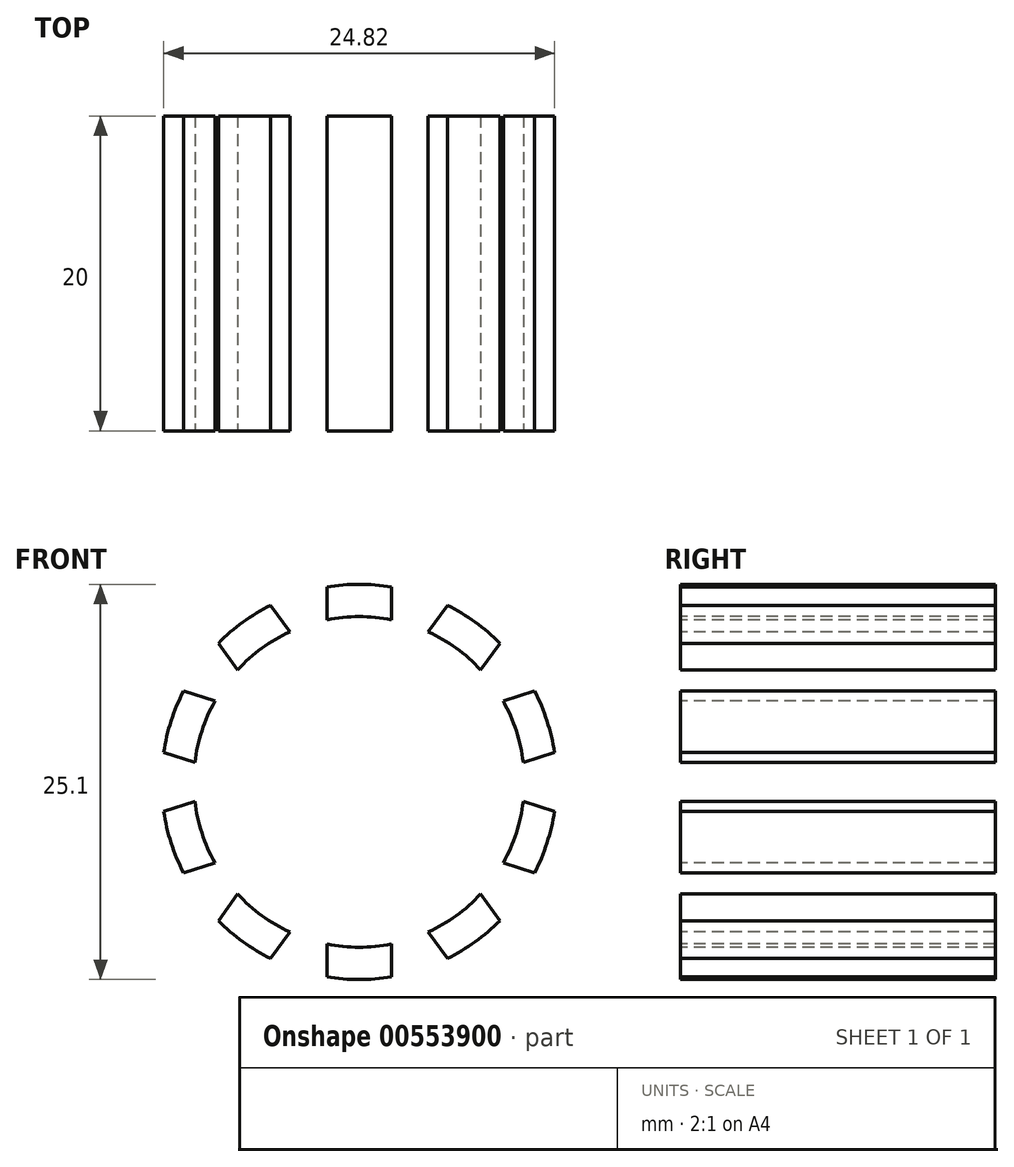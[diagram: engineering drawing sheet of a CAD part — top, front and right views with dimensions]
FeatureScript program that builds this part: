
annotation { "Feature Type Name" : "Feature", "Feature Type Description" : "" }
export const myFeature = defineFeature(function(context is Context, id is Id, definition is map)
    precondition{}
    {
        {
            var Q0;
            Q0=qCreatedBy(makeId("Front.planeOp"),FACE);
            var sketch = newSketch(context, id + "F0", { "sketchPlane" : qUnion([Q0])});
            skCircle(sketch, "E0", {"center": v(0, 0) * mm, "radius": 50 * mm});
            skLineSegment(sketch, "E1", {"start": v(0, 46.5) * mm, "end": v(83.9, 46.5) * mm, "construction": true});
            skLineSegment(sketch, "E2", {"start": v(0, 50) * mm, "end": v(23.37, 50) * mm, "construction": true});
            skArc(sketch, "E3.trimOffspring", {"start": v(-5.04, 60.29) * mm, "mid": v(-5.7, 54.98) * mm, "end": v(-6.05, 49.63) * mm});
            skLineSegment(sketch, "E4", {"start": v(0, 50) * mm, "end": v(0, 60.5) * mm});
            skArc(sketch, "E5.trimOffspring", {"start": v(0, 60.5) * mm, "mid": v(-2.52, 60.45) * mm, "end": v(-5.04, 60.29) * mm});
            skArc(sketch, "E6.MirrorCS", {"start": v(0, 60.5) * mm, "mid": v(2.52, 60.45) * mm, "end": v(5.04, 60.29) * mm});
            skArc(sketch, "E7.MirrorCS", {"start": v(5.04, 60.29) * mm, "mid": v(5.7, 54.98) * mm, "end": v(6.05, 49.63) * mm});
            skArc(sketch, "E8.1.0", {"start": v(-29.12, 53.03) * mm, "mid": v(-27.57, 47.9) * mm, "end": v(-25.71, 42.88) * mm});
            skArc(sketch, "E8.1.1", {"start": v(-24.6, 55.27) * mm, "mid": v(-26.89, 54.2) * mm, "end": v(-29.12, 53.03) * mm});
            skArc(sketch, "E8.1.2", {"start": v(-24.6, 55.27) * mm, "mid": v(-22.28, 56.25) * mm, "end": v(-19.92, 57.13) * mm});
            skArc(sketch, "E8.1.3", {"start": v(-19.92, 57.13) * mm, "mid": v(-17.15, 52.54) * mm, "end": v(-14.66, 47.8) * mm});
            skArc(sketch, "E9.3.2.0", {"start": v(-48.17, 36.6) * mm, "mid": v(-44.67, 32.55) * mm, "end": v(-40.93, 28.72) * mm});
            skArc(sketch, "E9.4.2.0", {"start": v(-44.96, 40.48) * mm, "mid": v(-46.6, 38.57) * mm, "end": v(-48.17, 36.6) * mm});
            skArc(sketch, "E9.8.2.0", {"start": v(-44.96, 40.48) * mm, "mid": v(-43.23, 42.32) * mm, "end": v(-41.43, 44.09) * mm});
            skArc(sketch, "E9.12.2.0", {"start": v(-41.43, 44.09) * mm, "mid": v(-37.04, 41.02) * mm, "end": v(-32.84, 37.7) * mm});
            skArc(sketch, "E9.3.3.0", {"start": v(-58.9, 13.84) * mm, "mid": v(-54.05, 11.57) * mm, "end": v(-49.07, 9.59) * mm});
            skArc(sketch, "E9.4.3.0", {"start": v(-57.54, 18.7) * mm, "mid": v(-58.27, 16.28) * mm, "end": v(-58.9, 13.84) * mm});
            skArc(sketch, "E9.8.3.0", {"start": v(-57.54, 18.7) * mm, "mid": v(-56.7, 21.08) * mm, "end": v(-55.78, 23.42) * mm});
            skArc(sketch, "E9.12.3.0", {"start": v(-55.78, 23.42) * mm, "mid": v(-50.52, 22.4) * mm, "end": v(-45.34, 21.09) * mm});
            skArc(sketch, "E9.3.4.0", {"start": v(-59.43, -11.31) * mm, "mid": v(-54.08, -11.42) * mm, "end": v(-48.73, -11.2) * mm});
            skArc(sketch, "E9.4.4.0", {"start": v(-60.17, -6.32) * mm, "mid": v(-59.85, -8.83) * mm, "end": v(-59.43, -11.31) * mm});
            skArc(sketch, "E9.8.4.0", {"start": v(-60.17, -6.32) * mm, "mid": v(-60.38, -3.81) * mm, "end": v(-60.49, -1.3) * mm});
            skArc(sketch, "E9.12.4.0", {"start": v(-60.49, -1.3) * mm, "mid": v(-55.27, -0.08) * mm, "end": v(-50, 0.82) * mm});
            skArc(sketch, "E9.3.5.0", {"start": v(-49.7, -34.5) * mm, "mid": v(-44.76, -32.42) * mm, "end": v(-39.96, -30.05) * mm});
            skArc(sketch, "E9.4.5.0", {"start": v(-52.4, -30.25) * mm, "mid": v(-51.09, -32.4) * mm, "end": v(-49.7, -34.5) * mm});
            skArc(sketch, "E9.8.5.0", {"start": v(-52.4, -30.25) * mm, "mid": v(-53.6, -28.04) * mm, "end": v(-54.73, -25.78) * mm});
            skArc(sketch, "E9.12.5.0", {"start": v(-54.73, -25.78) * mm, "mid": v(-50.46, -22.55) * mm, "end": v(-46, -19.58) * mm});
            skArc(sketch, "E9.3.6.0", {"start": v(-31.36, -51.74) * mm, "mid": v(-27.7, -47.83) * mm, "end": v(-24.28, -43.7) * mm});
            skArc(sketch, "E9.4.6.0", {"start": v(-35.56, -48.95) * mm, "mid": v(-33.5, -50.38) * mm, "end": v(-31.36, -51.74) * mm});
            skArc(sketch, "E9.8.6.0", {"start": v(-35.56, -48.95) * mm, "mid": v(-37.57, -47.42) * mm, "end": v(-39.51, -45.81) * mm});
            skArc(sketch, "E9.12.6.0", {"start": v(-39.51, -45.81) * mm, "mid": v(-36.93, -41.13) * mm, "end": v(-34.06, -36.6) * mm});
            skArc(sketch, "E9.3.7.0", {"start": v(-7.6, -60.02) * mm, "mid": v(-5.85, -54.96) * mm, "end": v(-4.4, -49.8) * mm});
            skArc(sketch, "E9.4.7.0", {"start": v(-12.58, -59.18) * mm, "mid": v(-10.1, -59.65) * mm, "end": v(-7.6, -60.02) * mm});
            skArc(sketch, "E9.8.7.0", {"start": v(-12.58, -59.18) * mm, "mid": v(-15.03, -58.6) * mm, "end": v(-17.46, -57.93) * mm});
            skArc(sketch, "E9.12.7.0", {"start": v(-17.46, -57.93) * mm, "mid": v(-17, -52.6) * mm, "end": v(-16.23, -47.3) * mm});
            skArc(sketch, "E9.3.8.0", {"start": v(17.46, -57.93) * mm, "mid": v(17, -52.6) * mm, "end": v(16.23, -47.3) * mm});
            skArc(sketch, "E9.4.8.0", {"start": v(12.58, -59.18) * mm, "mid": v(15.03, -58.6) * mm, "end": v(17.46, -57.93) * mm});
            skArc(sketch, "E9.8.8.0", {"start": v(12.58, -59.18) * mm, "mid": v(10.1, -59.65) * mm, "end": v(7.6, -60.02) * mm});
            skArc(sketch, "E9.12.8.0", {"start": v(7.6, -60.02) * mm, "mid": v(5.85, -54.96) * mm, "end": v(4.4, -49.8) * mm});
            skArc(sketch, "E9.3.9.0", {"start": v(39.51, -45.81) * mm, "mid": v(36.93, -41.13) * mm, "end": v(34.06, -36.6) * mm});
            skArc(sketch, "E9.4.9.0", {"start": v(35.56, -48.95) * mm, "mid": v(37.57, -47.42) * mm, "end": v(39.51, -45.81) * mm});
            skArc(sketch, "E9.8.9.0", {"start": v(35.56, -48.95) * mm, "mid": v(33.5, -50.38) * mm, "end": v(31.36, -51.74) * mm});
            skArc(sketch, "E9.12.9.0", {"start": v(31.36, -51.74) * mm, "mid": v(27.7, -47.83) * mm, "end": v(24.28, -43.7) * mm});
            skArc(sketch, "E9.3.10.0", {"start": v(54.73, -25.78) * mm, "mid": v(50.46, -22.55) * mm, "end": v(46, -19.58) * mm});
            skArc(sketch, "E9.4.10.0", {"start": v(52.4, -30.25) * mm, "mid": v(53.6, -28.04) * mm, "end": v(54.73, -25.78) * mm});
            skArc(sketch, "E9.8.10.0", {"start": v(52.4, -30.25) * mm, "mid": v(51.09, -32.4) * mm, "end": v(49.7, -34.5) * mm});
            skArc(sketch, "E9.12.10.0", {"start": v(49.7, -34.5) * mm, "mid": v(44.76, -32.42) * mm, "end": v(39.96, -30.05) * mm});
            skArc(sketch, "E9.3.11.0", {"start": v(60.49, -1.3) * mm, "mid": v(55.27, -0.08) * mm, "end": v(50, 0.82) * mm});
            skArc(sketch, "E9.4.11.0", {"start": v(60.17, -6.32) * mm, "mid": v(60.38, -3.81) * mm, "end": v(60.49, -1.3) * mm});
            skArc(sketch, "E9.8.11.0", {"start": v(60.17, -6.32) * mm, "mid": v(59.85, -8.83) * mm, "end": v(59.43, -11.31) * mm});
            skArc(sketch, "E9.12.11.0", {"start": v(59.43, -11.31) * mm, "mid": v(54.08, -11.42) * mm, "end": v(48.73, -11.2) * mm});
            skArc(sketch, "E9.3.12.0", {"start": v(55.78, 23.42) * mm, "mid": v(50.52, 22.4) * mm, "end": v(45.34, 21.09) * mm});
            skArc(sketch, "E9.4.12.0", {"start": v(57.54, 18.7) * mm, "mid": v(56.7, 21.08) * mm, "end": v(55.78, 23.42) * mm});
            skArc(sketch, "E9.8.12.0", {"start": v(57.54, 18.7) * mm, "mid": v(58.27, 16.28) * mm, "end": v(58.9, 13.84) * mm});
            skArc(sketch, "E9.12.12.0", {"start": v(58.9, 13.84) * mm, "mid": v(54.05, 11.57) * mm, "end": v(49.07, 9.59) * mm});
            skArc(sketch, "E9.3.13.0", {"start": v(41.43, 44.09) * mm, "mid": v(37.04, 41.02) * mm, "end": v(32.84, 37.7) * mm});
            skArc(sketch, "E9.4.13.0", {"start": v(44.96, 40.48) * mm, "mid": v(43.23, 42.32) * mm, "end": v(41.43, 44.09) * mm});
            skArc(sketch, "E9.8.13.0", {"start": v(44.96, 40.48) * mm, "mid": v(46.6, 38.57) * mm, "end": v(48.17, 36.6) * mm});
            skArc(sketch, "E9.12.13.0", {"start": v(48.17, 36.6) * mm, "mid": v(44.67, 32.55) * mm, "end": v(40.93, 28.72) * mm});
            skArc(sketch, "E9.3.14.0", {"start": v(19.92, 57.13) * mm, "mid": v(17.15, 52.54) * mm, "end": v(14.66, 47.8) * mm});
            skArc(sketch, "E9.4.14.0", {"start": v(24.6, 55.27) * mm, "mid": v(22.28, 56.25) * mm, "end": v(19.92, 57.13) * mm});
            skArc(sketch, "E9.8.14.0", {"start": v(24.6, 55.27) * mm, "mid": v(26.89, 54.2) * mm, "end": v(29.12, 53.03) * mm});
            skArc(sketch, "E9.12.14.0", {"start": v(29.12, 53.03) * mm, "mid": v(27.57, 47.9) * mm, "end": v(25.71, 42.88) * mm});
            skSolve(sketch);
        }
        {
            var Q0;
            Q0 = qSketchRegion(id + "F0", true);
            extrude(context, id + "F1", {"entities" : qUnion([Q0]), "depth" : 20 * mm, "offsetDistance" : 25 * mm});
        }
        {
            var Q0;
            Q0=makeQuery(id+"F1.opExtrude","CAP_FACE",FACE,{"disambiguationData":[OSD([sQuery(id+"F0.wireOp",EDGE,"E0"),sQuery(id+"F0.wireOp",EDGE,"E3.trimOffspring"),sQuery(id+"F0.wireOp",EDGE,"E5.trimOffspring"),sQuery(id+"F0.wireOp",EDGE,"E6.MirrorCS"),sQuery(id+"F0.wireOp",EDGE,"E7.MirrorCS"),sQuery(id+"F0.wireOp",EDGE,"E8.1.0"),sQuery(id+"F0.wireOp",EDGE,"E8.1.1"),sQuery(id+"F0.wireOp",EDGE,"E8.1.2"),sQuery(id+"F0.wireOp",EDGE,"E8.1.3"),sQuery(id+"F0.wireOp",EDGE,"E9.3.2.0"),sQuery(id+"F0.wireOp",EDGE,"E9.4.2.0"),sQuery(id+"F0.wireOp",EDGE,"E9.8.2.0"),sQuery(id+"F0.wireOp",EDGE,"E9.12.2.0"),sQuery(id+"F0.wireOp",EDGE,"E9.3.3.0"),sQuery(id+"F0.wireOp",EDGE,"E9.4.3.0"),sQuery(id+"F0.wireOp",EDGE,"E9.8.3.0"),sQuery(id+"F0.wireOp",EDGE,"E9.12.3.0"),sQuery(id+"F0.wireOp",EDGE,"E9.3.4.0"),sQuery(id+"F0.wireOp",EDGE,"E9.4.4.0"),sQuery(id+"F0.wireOp",EDGE,"E9.8.4.0"),sQuery(id+"F0.wireOp",EDGE,"E9.12.4.0"),sQuery(id+"F0.wireOp",EDGE,"E9.3.5.0"),sQuery(id+"F0.wireOp",EDGE,"E9.4.5.0"),sQuery(id+"F0.wireOp",EDGE,"E9.8.5.0"),sQuery(id+"F0.wireOp",EDGE,"E9.12.5.0"),sQuery(id+"F0.wireOp",EDGE,"E9.3.6.0"),sQuery(id+"F0.wireOp",EDGE,"E9.4.6.0"),sQuery(id+"F0.wireOp",EDGE,"E9.8.6.0"),sQuery(id+"F0.wireOp",EDGE,"E9.12.6.0"),sQuery(id+"F0.wireOp",EDGE,"E9.3.7.0"),sQuery(id+"F0.wireOp",EDGE,"E9.4.7.0"),sQuery(id+"F0.wireOp",EDGE,"E9.8.7.0"),sQuery(id+"F0.wireOp",EDGE,"E9.12.7.0"),sQuery(id+"F0.wireOp",EDGE,"E9.3.8.0"),sQuery(id+"F0.wireOp",EDGE,"E9.4.8.0"),sQuery(id+"F0.wireOp",EDGE,"E9.8.8.0"),sQuery(id+"F0.wireOp",EDGE,"E9.12.8.0"),sQuery(id+"F0.wireOp",EDGE,"E9.3.9.0"),sQuery(id+"F0.wireOp",EDGE,"E9.4.9.0"),sQuery(id+"F0.wireOp",EDGE,"E9.8.9.0"),sQuery(id+"F0.wireOp",EDGE,"E9.12.9.0"),sQuery(id+"F0.wireOp",EDGE,"E9.3.10.0"),sQuery(id+"F0.wireOp",EDGE,"E9.4.10.0"),sQuery(id+"F0.wireOp",EDGE,"E9.8.10.0"),sQuery(id+"F0.wireOp",EDGE,"E9.12.10.0"),sQuery(id+"F0.wireOp",EDGE,"E9.3.11.0"),sQuery(id+"F0.wireOp",EDGE,"E9.4.11.0"),sQuery(id+"F0.wireOp",EDGE,"E9.8.11.0"),sQuery(id+"F0.wireOp",EDGE,"E9.12.11.0"),sQuery(id+"F0.wireOp",EDGE,"E9.3.12.0"),sQuery(id+"F0.wireOp",EDGE,"E9.4.12.0"),sQuery(id+"F0.wireOp",EDGE,"E9.8.12.0"),sQuery(id+"F0.wireOp",EDGE,"E9.12.12.0"),sQuery(id+"F0.wireOp",EDGE,"E9.3.13.0"),sQuery(id+"F0.wireOp",EDGE,"E9.4.13.0"),sQuery(id+"F0.wireOp",EDGE,"E9.8.13.0"),sQuery(id+"F0.wireOp",EDGE,"E9.12.13.0"),sQuery(id+"F0.wireOp",EDGE,"E9.3.14.0"),sQuery(id+"F0.wireOp",EDGE,"E9.4.14.0"),sQuery(id+"F0.wireOp",EDGE,"E9.8.14.0"),sQuery(id+"F0.wireOp",EDGE,"E9.12.14.0")])],"isStart":false});
            var sketch = newSketch(context, id + "F2", { "sketchPlane" : qUnion([Q0])});
            skArc(sketch, "E10", {"start": v(2.05, 12.38) * mm, "mid": v(0, 12.55) * mm, "end": v(-2.05, 12.38) * mm});
            skCircle(sketch, "E11", {"center": v(0, 0) * mm, "radius": 10.5 * mm});
            skLineSegment(sketch, "E12", {"start": v(-2.05, 12.38) * mm, "end": v(-2.05, 10.3) * mm});
            skLineSegment(sketch, "E13", {"start": v(2.05, 12.38) * mm, "end": v(2.05, 10.3) * mm});
            skLineSegment(sketch, "E14.1.0", {"start": v(-8.94, 8.81) * mm, "end": v(-7.71, 7.13) * mm});
            skArc(sketch, "E14.1.1", {"start": v(-5.62, 11.22) * mm, "mid": v(-7.38, 10.15) * mm, "end": v(-8.94, 8.81) * mm});
            skLineSegment(sketch, "E14.1.2", {"start": v(-5.62, 11.22) * mm, "end": v(-4.4, 9.54) * mm});
            skLineSegment(sketch, "E14.2.0", {"start": v(-12.4, 1.88) * mm, "end": v(-10.43, 1.23) * mm});
            skArc(sketch, "E14.2.1", {"start": v(-11.14, 5.78) * mm, "mid": v(-11.94, 3.88) * mm, "end": v(-12.4, 1.88) * mm});
            skLineSegment(sketch, "E14.2.2", {"start": v(-11.14, 5.78) * mm, "end": v(-9.16, 5.13) * mm});
            skLineSegment(sketch, "E14.3.0", {"start": v(-11.14, -5.78) * mm, "end": v(-9.16, -5.13) * mm});
            skArc(sketch, "E14.3.1", {"start": v(-12.4, -1.88) * mm, "mid": v(-11.94, -3.88) * mm, "end": v(-11.14, -5.78) * mm});
            skLineSegment(sketch, "E14.3.2", {"start": v(-12.4, -1.88) * mm, "end": v(-10.43, -1.23) * mm});
            skLineSegment(sketch, "E14.4.0", {"start": v(-5.62, -11.22) * mm, "end": v(-4.4, -9.54) * mm});
            skArc(sketch, "E14.4.1", {"start": v(-8.94, -8.81) * mm, "mid": v(-7.38, -10.15) * mm, "end": v(-5.62, -11.22) * mm});
            skLineSegment(sketch, "E14.4.2", {"start": v(-8.94, -8.81) * mm, "end": v(-7.71, -7.13) * mm});
            skLineSegment(sketch, "E14.5.0", {"start": v(2.05, -12.38) * mm, "end": v(2.05, -10.3) * mm});
            skArc(sketch, "E14.5.1", {"start": v(-2.05, -12.38) * mm, "mid": v(0, -12.55) * mm, "end": v(2.05, -12.38) * mm});
            skLineSegment(sketch, "E14.5.2", {"start": v(-2.05, -12.38) * mm, "end": v(-2.05, -10.3) * mm});
            skLineSegment(sketch, "E14.6.0", {"start": v(8.94, -8.81) * mm, "end": v(7.71, -7.13) * mm});
            skArc(sketch, "E14.6.1", {"start": v(5.62, -11.22) * mm, "mid": v(7.38, -10.15) * mm, "end": v(8.94, -8.81) * mm});
            skLineSegment(sketch, "E14.6.2", {"start": v(5.62, -11.22) * mm, "end": v(4.4, -9.54) * mm});
            skLineSegment(sketch, "E14.7.0", {"start": v(12.4, -1.88) * mm, "end": v(10.43, -1.23) * mm});
            skArc(sketch, "E14.7.1", {"start": v(11.14, -5.78) * mm, "mid": v(11.94, -3.88) * mm, "end": v(12.4, -1.88) * mm});
            skLineSegment(sketch, "E14.7.2", {"start": v(11.14, -5.78) * mm, "end": v(9.16, -5.13) * mm});
            skLineSegment(sketch, "E14.8.0", {"start": v(11.14, 5.78) * mm, "end": v(9.16, 5.13) * mm});
            skArc(sketch, "E14.8.1", {"start": v(12.4, 1.88) * mm, "mid": v(11.94, 3.88) * mm, "end": v(11.14, 5.78) * mm});
            skLineSegment(sketch, "E14.8.2", {"start": v(12.4, 1.88) * mm, "end": v(10.43, 1.23) * mm});
            skLineSegment(sketch, "E14.9.0", {"start": v(5.62, 11.22) * mm, "end": v(4.4, 9.54) * mm});
            skArc(sketch, "E14.9.1", {"start": v(8.94, 8.81) * mm, "mid": v(7.38, 10.15) * mm, "end": v(5.62, 11.22) * mm});
            skLineSegment(sketch, "E14.9.2", {"start": v(8.94, 8.81) * mm, "end": v(7.71, 7.13) * mm});
            skSolve(sketch);
        }
        {
            var Q0;
            Q0=makeQuery(id+"F2.imprint","IMPRINT",FACE,{"disambiguationData":[TD([[makeQuery(id+"F2.imprint","IMPRINT",EDGE,{"derivedFrom":sQuery(id+"F2.wireOp",EDGE,"E10")}),-1.0]])]});
            var Q1;
            {var subQ0=sQuery(id+"F2.wireOp",EDGE,"E11");var subQ8=makeQuery(id+"F2.imprint","INTERSECT",VERTEX,{"derivedFrom":[subQ0,sQuery(id+"F2.wireOp",EDGE,"E14.8.0")]});Q1=makeQuery(id+"F2.imprint","IMPRINT",FACE,{"disambiguationData":[TD([[makeQuery(id+"F2.imprint","IMPRINT",EDGE,{"disambiguationData":[TD([[subQ8,1.0]])],"derivedFrom":subQ0}),1.0]])]});}
            extrude(context, id + "F3", {"entities" : qUnion([Q0, Q1]), "operationType" : NewBodyOperationType.REMOVE, "oppositeDirection" : true, "depth" : 25 * mm, "offsetDistance" : 25 * mm});
        }
    });
